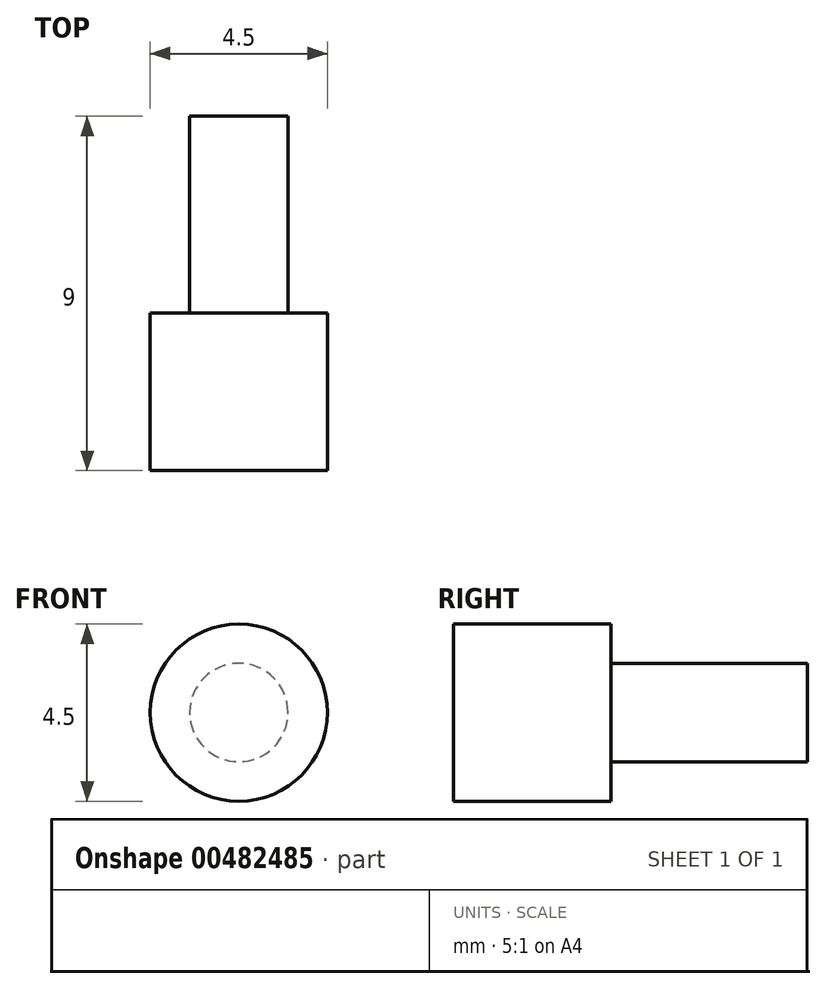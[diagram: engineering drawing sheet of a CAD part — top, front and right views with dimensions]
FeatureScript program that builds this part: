
annotation { "Feature Type Name" : "Feature", "Feature Type Description" : "" }
export const myFeature = defineFeature(function(context is Context, id is Id, definition is map)
    precondition{}
    {
        {
            var Q0;
            Q0=qCreatedBy(makeId("Front.planeOp"),FACE);
            var sketch = newSketch(context, id + "F0", { "sketchPlane" : qUnion([Q0])});
            skCircle(sketch, "E0", {"center": v(-47.02, -8.77) * mm, "radius": 1.25 * mm});
            skSolve(sketch);
        }
        {
            var Q0;
            Q0 = qSketchRegion(id + "F0", true);
            extrude(context, id + "F1", {"entities" : qUnion([Q0]), "depth" : 5 * mm, "offsetDistance" : 25 * mm});
        }
        {
            var Q0;
            Q0=makeQuery(id+"F1.opExtrude","CAP_FACE",FACE,{"disambiguationData":[OSD([sQuery(id+"F0.wireOp",EDGE,"E0")])],"isStart":false});
            var sketch = newSketch(context, id + "F2", { "sketchPlane" : qUnion([Q0])});
            skCircle(sketch, "E1", {"center": v(-47.02, -8.77) * mm, "radius": 2.25 * mm});
            skSolve(sketch);
        }
        {
            var Q0;
            Q0=makeQuery(id+"F2.imprint","IMPRINT",FACE,{"disambiguationData":[TD([[makeQuery(id+"F2.imprint","IMPRINT",EDGE,{"derivedFrom":makeQuery(id+"F1.opExtrude","CAP_EDGE",EDGE,{"disambiguationData":[OSD([sQuery(id+"F0.wireOp",EDGE,"E0")])],"isStart":false})}),1.0]])]});
            var Q1;
            Q1=makeQuery(id+"F2.imprint","IMPRINT",FACE,{"disambiguationData":[TD([[makeQuery(id+"F2.imprint","IMPRINT",EDGE,{"derivedFrom":sQuery(id+"F2.wireOp",EDGE,"E1")}),1.0]])]});
            extrude(context, id + "F3", {"entities" : qUnion([Q0, Q1]), "operationType" : NewBodyOperationType.ADD, "depth" : 4 * mm, "offsetDistance" : 25 * mm});
        }
    });
